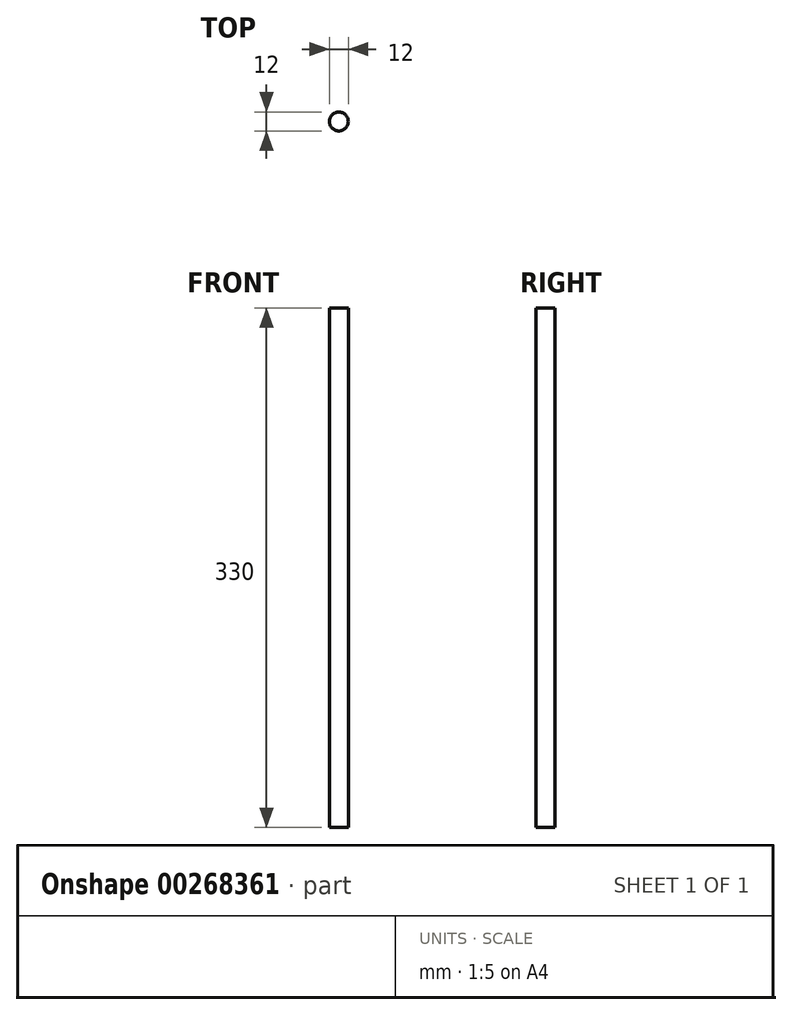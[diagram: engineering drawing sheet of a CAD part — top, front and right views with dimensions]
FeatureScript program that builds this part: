
annotation { "Feature Type Name" : "Feature", "Feature Type Description" : "" }
export const myFeature = defineFeature(function(context is Context, id is Id, definition is map)
    precondition{}
    {
        {
            var Q0;
            Q0=qCreatedBy(makeId("Top.planeOp"),FACE);
            var sketch = newSketch(context, id + "F0", { "sketchPlane" : qUnion([Q0])});
            skCircle(sketch, "E0", {"center": v(0, 0) * mm, "radius": 6 * mm});
            skSolve(sketch);
        }
        {
            var Q0;
            Q0=qSketchRegion(id+"F0",true);
            extrude(context, id + "F1", {"entities" : qUnion([Q0]), "depth" : 330 * mm});
        }
    });
